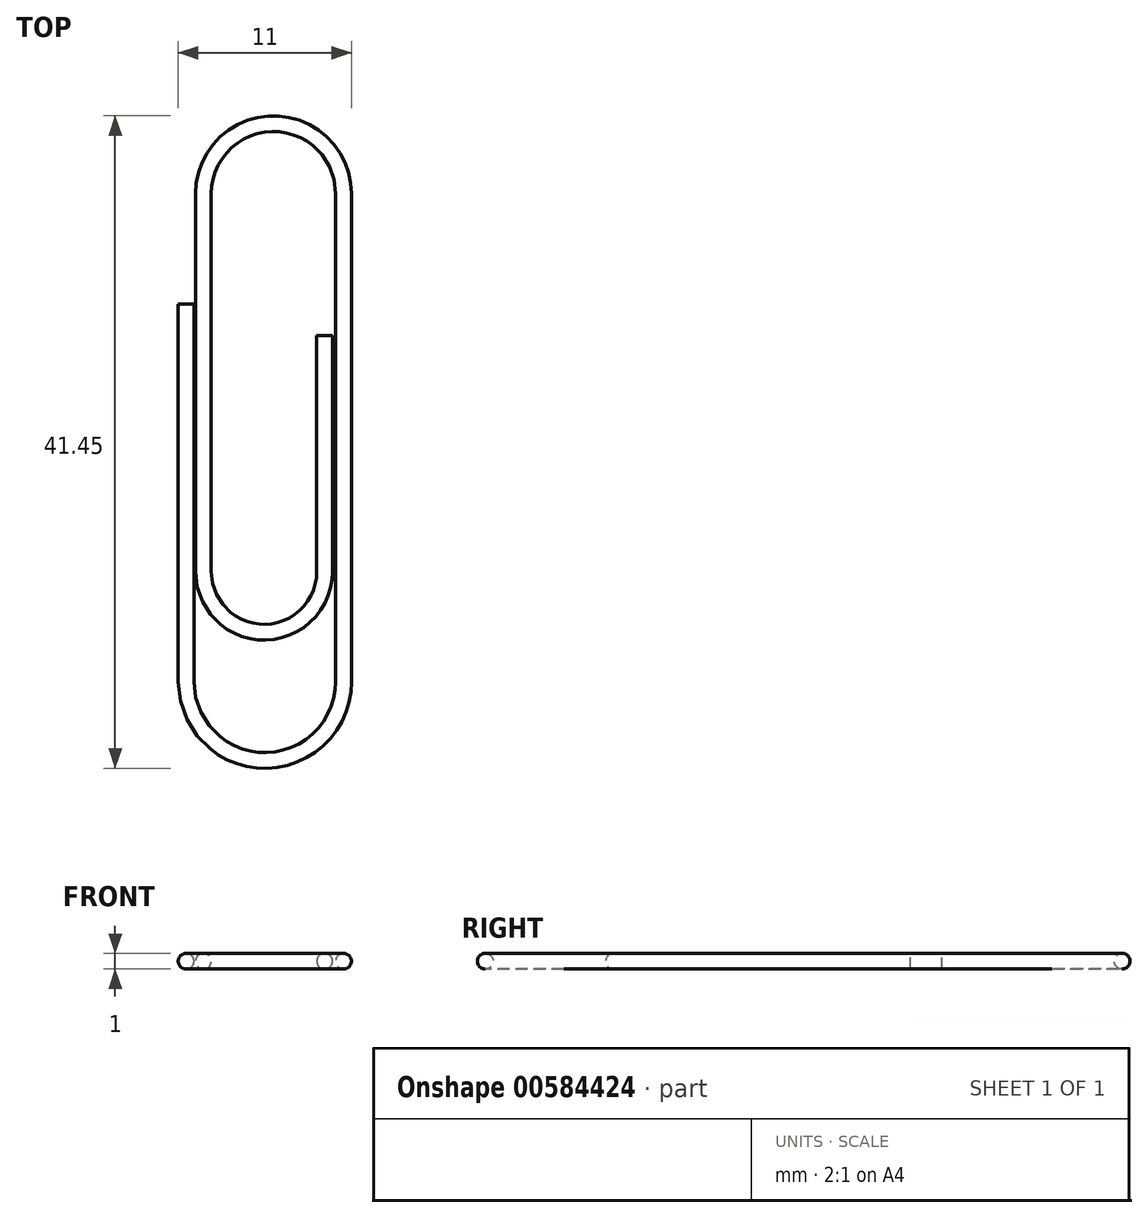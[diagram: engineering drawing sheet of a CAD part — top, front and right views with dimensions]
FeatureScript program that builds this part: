
annotation { "Feature Type Name" : "Feature", "Feature Type Description" : "" }
export const myFeature = defineFeature(function(context is Context, id is Id, definition is map)
    precondition{}
    {
        {
            var Q0;
            Q0=qCreatedBy(makeId("Top.planeOp"),FACE);
            var sketch = newSketch(context, id + "F0", { "sketchPlane" : qUnion([Q0])});
            skLineSegment(sketch, "E0", {"start": v(8.8, -17) * mm, "end": v(8.8, -2) * mm});
            skLineSegment(sketch, "E1", {"start": v(1.1, -17) * mm, "end": v(1.1, 7) * mm});
            skArc(sketch, "E2", {"start": v(1.1, -17) * mm, "mid": v(4.95, -20.85) * mm, "end": v(8.8, -17) * mm});
            skLineSegment(sketch, "E3", {"start": v(10, 7) * mm, "end": v(10, -24) * mm});
            skArc(sketch, "E4", {"start": v(10, 7) * mm, "mid": v(5.55, 11.45) * mm, "end": v(1.1, 7) * mm});
            skLineSegment(sketch, "E5", {"start": v(0, -24) * mm, "end": v(0, 0) * mm});
            skArc(sketch, "E6", {"start": v(0, -24) * mm, "mid": v(5, -29) * mm, "end": v(10, -24) * mm});
            skSolve(sketch);
        }
        {
            var Q0;
            Q0=qCreatedBy(makeId("Front.planeOp"),FACE);
            var sketch = newSketch(context, id + "F1", { "sketchPlane" : qUnion([Q0])});
            skCircle(sketch, "E7", {"center": v(0, 0) * mm, "radius": 0.5 * mm});
            skSolve(sketch);
        }
        {
            var Q0;
            Q0 = qSketchRegion(id + "F1", true);
            var Q1;
            Q1 = qConstructionFilter(qBodyType(qCreatedBy(id + "F0" ,EDGE), BodyType.WIRE), ConstructionObject.NO);
            sweep(context, id + "F2", {"profiles" : qUnion([Q0]), "path" : qUnion([Q1])});
        }
    });
